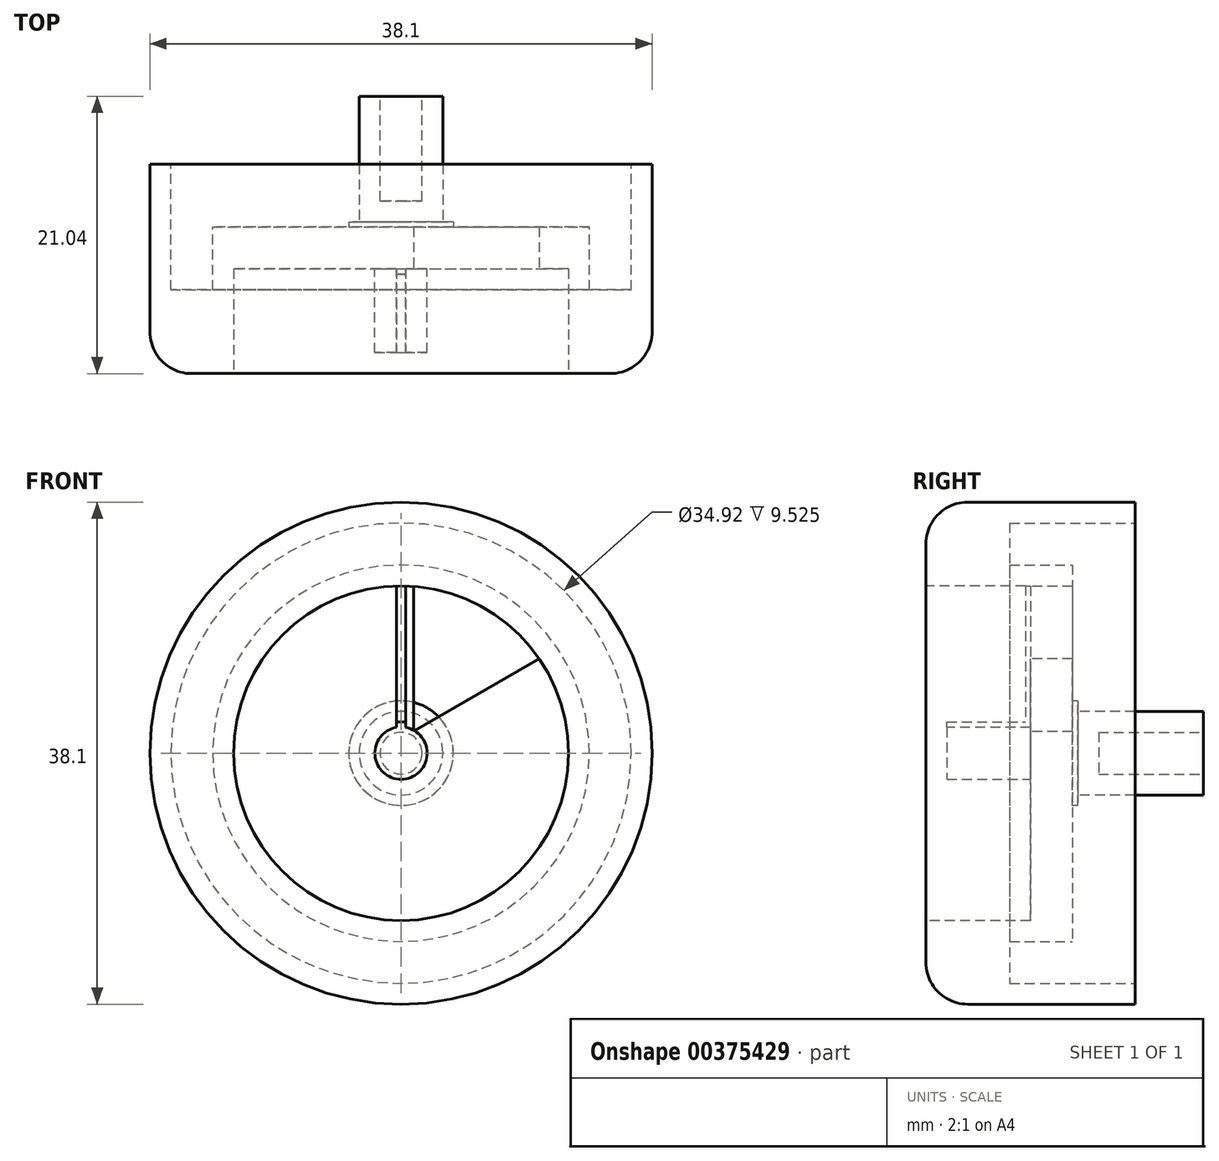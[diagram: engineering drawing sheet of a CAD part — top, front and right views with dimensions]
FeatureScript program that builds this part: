
annotation { "Feature Type Name" : "Feature", "Feature Type Description" : "" }
export const myFeature = defineFeature(function(context is Context, id is Id, definition is map)
    precondition{}
    {
        {
            var Q0;
            Q0=qCreatedBy(makeId("Front.planeOp"),FACE);
            var sketch = newSketch(context, id + "F0", { "sketchPlane" : qUnion([Q0])});
            skCircle(sketch, "E0", {"center": v(0, 0) * mm, "radius": 19.05 * mm});
            skSolve(sketch);
        }
        {
            var Q0;
            Q0=qSketchRegion(id+"F0",true);
            extrude(context, id + "F1", {"entities" : qUnion([Q0]), "depth" : 15.88 * mm, "symmetric" : true});
        }
        {
            var Q0;
            Q0=makeQuery(id+"F1.opExtrude","CAP_FACE",FACE,{"disambiguationData":[OSD([sQuery(id+"F0.wireOp",EDGE,"E0")])],"isStart":false});
            var sketch = newSketch(context, id + "F2", { "sketchPlane" : qUnion([Q0])});
            skCircle(sketch, "E1", {"center": v(0, 0) * mm, "radius": 12.7 * mm});
            skSolve(sketch);
        }
        {
            var Q0;
            Q0=qSketchRegion(id+"F2",true);
            extrude(context, id + "F3", {"entities" : qUnion([Q0]), "operationType" : NewBodyOperationType.REMOVE, "oppositeDirection" : true, "depth" : 7.94 * mm});
        }
        {
            var Q0;
            Q0=makeQuery(id+"F3.boolean.opBoolean","COPY",FACE,{"derivedFrom":makeQuery(id+"F3.opExtrude","CAP_FACE",FACE,{"disambiguationData":[OSD([sQuery(id+"F2.wireOp",EDGE,"E1")])],"isStart":false})});
            var sketch = newSketch(context, id + "F4", { "sketchPlane" : qUnion([Q0])});
            skLineSegment(sketch, "E2", {"start": v(0, 13.75) * mm, "end": v(0, 0) * mm, "construction": true});
            skLineSegment(sketch, "E3", {"start": v(0, 0) * mm, "end": v(12.12, 7) * mm, "construction": true});
            skLineSegment(sketch, "E4", {"start": v(0.95, 12.66) * mm, "end": v(0.95, 1.65) * mm});
            skLineSegment(sketch, "E5", {"start": v(0.95, 1.65) * mm, "end": v(10.5, 7.16) * mm});
            skArc(sketch, "E6.0", {"start": v(10.5, 7.16) * mm, "mid": v(6.35, 11) * mm, "end": v(0.95, 12.66) * mm});
            skLineSegment(sketch, "E7", {"start": v(0, 0) * mm, "end": v(9.55, 16.55) * mm, "construction": true});
            skSolve(sketch);
        }
        {
            var Q0;
            Q0=qSketchRegion(id+"F4",true);
            extrude(context, id + "F5", {"entities" : qUnion([Q0]), "operationType" : NewBodyOperationType.REMOVE, "endBound" : BoundingType.THROUGH_ALL, "oppositeDirection" : true, "depth" : 25.4 * mm});
        }
        {
            var Q0;
            Q0=makeQuery(id+"F1.opExtrude","CAP_FACE",FACE,{"disambiguationData":[OSD([sQuery(id+"F0.wireOp",EDGE,"E0")])],"isStart":true});
            var sketch = newSketch(context, id + "F6", { "sketchPlane" : qUnion([Q0])});
            skCircle(sketch, "E8", {"center": v(0, 0) * mm, "radius": 12.7 * mm});
            skSolve(sketch);
        }
        {
            var Q0;
            Q0=qSketchRegion(id+"F6",true);
            extrude(context, id + "F7", {"entities" : qUnion([Q0]), "operationType" : NewBodyOperationType.REMOVE, "oppositeDirection" : true, "depth" : 4.76 * mm});
        }
        {
            var Q0;
            Q0=makeQuery(id+"F7.boolean.opBoolean","COPY",FACE,{"derivedFrom":makeQuery(id+"F7.opExtrude","CAP_FACE",FACE,{"disambiguationData":[OSD([sQuery(id+"F6.wireOp",EDGE,"E8")])],"isStart":false})});
            var sketch = newSketch(context, id + "F8", { "sketchPlane" : qUnion([Q0])});
            skCircle(sketch, "E9", {"center": v(0, 0) * mm, "radius": 3.97 * mm});
            skSolve(sketch);
        }
        {
            var Q0;
            Q0=qSketchRegion(id+"F8",true);
            extrude(context, id + "F9", {"entities" : qUnion([Q0]), "operationType" : NewBodyOperationType.ADD, "depth" : 0.4 * mm});
        }
        {
            var Q0;
            Q0=makeQuery(id+"F9.opExtrude","CAP_FACE",FACE,{"disambiguationData":[OSD([sQuery(id+"F8.wireOp",EDGE,"E9")])],"isStart":false});
            var sketch = newSketch(context, id + "F10", { "sketchPlane" : qUnion([Q0])});
            skCircle(sketch, "E10", {"center": v(0, 0) * mm, "radius": 3.17 * mm});
            skSolve(sketch);
        }
        {
            var Q0;
            Q0=qSketchRegion(id+"F10",true);
            extrude(context, id + "F11", {"entities" : qUnion([Q0]), "operationType" : NewBodyOperationType.ADD, "depth" : 9.52 * mm});
        }
        {
            var Q0;
            Q0=makeQuery(id+"F11.opExtrude","CAP_FACE",FACE,{"disambiguationData":[OSD([sQuery(id+"F10.wireOp",EDGE,"E10")])],"isStart":false});
            var sketch = newSketch(context, id + "F12", { "sketchPlane" : qUnion([Q0])});
            skCircle(sketch, "E11", {"center": v(0, 0) * mm, "radius": 1.59 * mm});
            skSolve(sketch);
        }
        {
            var Q0;
            Q0=qSketchRegion(id+"F12",true);
            extrude(context, id + "F13", {"entities" : qUnion([Q0]), "operationType" : NewBodyOperationType.REMOVE, "oppositeDirection" : true, "depth" : 7.94 * mm});
        }
        {
            var Q0;
            Q0=makeQuery(id+"F3.boolean.opBoolean","COPY",FACE,{"derivedFrom":makeQuery(id+"F3.opExtrude","CAP_FACE",FACE,{"disambiguationData":[OSD([sQuery(id+"F2.wireOp",EDGE,"E1")])],"isStart":false})});
            var sketch = newSketch(context, id + "F14", { "sketchPlane" : qUnion([Q0])});
            skCircle(sketch, "E12", {"center": v(0, 0) * mm, "radius": 1.98 * mm});
            skSolve(sketch);
        }
        {
            var Q0;
            Q0=qSketchRegion(id+"F14",true);
            extrude(context, id + "F15", {"entities" : qUnion([Q0]), "operationType" : NewBodyOperationType.ADD, "depth" : 6.35 * mm});
        }
        {
            var Q0;
            {var subQ2=sQuery(id+"F2.wireOp",EDGE,"E1");Q0=makeQuery(id+"F15.boolean.opBoolean","SPLIT",FACE,{"disambiguationData":[TD([makeQuery(id+"F5.boolean.opBoolean","COPY",FACE,{"derivedFrom":makeQuery(id+"F5.opExtrude","SWEPT_FACE",FACE,{"disambiguationData":[OSD([sQuery(id+"F4.wireOp",EDGE,"E4")])]})})])],"derivedFrom":makeQuery(id+"F3.boolean.opBoolean","COPY",FACE,{"derivedFrom":makeQuery(id+"F3.opExtrude","CAP_FACE",FACE,{"disambiguationData":[OSD([subQ2])],"isStart":false})})});}
            var sketch = newSketch(context, id + "F16", { "sketchPlane" : qUnion([Q0])});
            skLineSegment(sketch, "E13.bottom", {"start": v(-0.34, 12.7) * mm, "end": v(0.34, 12.7) * mm});
            skLineSegment(sketch, "E13.top", {"start": v(-0.34, 2.37) * mm, "end": v(0.34, 2.37) * mm});
            skLineSegment(sketch, "E13.left", {"start": v(-0.34, 12.7) * mm, "end": v(-0.34, 2.37) * mm});
            skLineSegment(sketch, "E13.right", {"start": v(0.34, 12.7) * mm, "end": v(0.34, 2.37) * mm});
            skSolve(sketch);
        }
        {
            var Q0;
            {var subQ0=sQuery(id+"F16.wireOp",EDGE,"E13.left");var subQ1=sQuery(id+"F16.wireOp",EDGE,"E13.top");var subQ2=makeQuery(id+"F16.imprint","INTERSECT",VERTEX,{"derivedFrom":[subQ1,subQ0]});Q0=makeQuery(id+"F16.imprint","IMPRINT",FACE,{"disambiguationData":[TD([[makeQuery(id+"F16.imprint","IMPRINT",EDGE,{"disambiguationData":[TD([[subQ2,-1.0]])],"derivedFrom":subQ1}),1.0]])]});}
            extrude(context, id + "F17", {"entities" : qUnion([Q0]), "operationType" : NewBodyOperationType.ADD, "depth" : 0.4 * mm});
        }
        {
            var Q0;
            Q0=makeQuery(id+"F15.opExtrude","CAP_FACE",FACE,{"disambiguationData":[OSD([sQuery(id+"F14.wireOp",EDGE,"E12")])],"isStart":false});
            var sketch = newSketch(context, id + "F18", { "sketchPlane" : qUnion([Q0])});
            skLineSegment(sketch, "E14.bottom", {"start": v(-0.34, 1.95) * mm, "end": v(0.34, 1.95) * mm});
            skLineSegment(sketch, "E14.top", {"start": v(-0.34, 2.36) * mm, "end": v(0.34, 2.36) * mm});
            skLineSegment(sketch, "E14.left", {"start": v(-0.34, 1.95) * mm, "end": v(-0.34, 2.36) * mm});
            skLineSegment(sketch, "E14.right", {"start": v(0.34, 1.95) * mm, "end": v(0.34, 2.36) * mm});
            skSolve(sketch);
        }
        {
            var Q0;
            Q0=qSketchRegion(id+"F18",true);
            extrude(context, id + "F19", {"entities" : qUnion([Q0]), "operationType" : NewBodyOperationType.ADD, "oppositeDirection" : true, "depth" : 6.35 * mm});
        }
        {
            var Q0;
            Q0=makeQuery(id+"F1.opExtrude","CAP_FACE",FACE,{"disambiguationData":[OSD([sQuery(id+"F0.wireOp",EDGE,"E0")])],"isStart":true});
            var sketch = newSketch(context, id + "F20", { "sketchPlane" : qUnion([Q0])});
            skCircle(sketch, "E15", {"center": v(0, 0) * mm, "radius": 17.46 * mm});
            skSolve(sketch);
        }
        {
            var Q0;
            Q0=makeQuery(id+"F20.imprint","IMPRINT",FACE,{"disambiguationData":[TD([[makeQuery(id+"F20.imprint","IMPRINT",EDGE,{"derivedFrom":sQuery(id+"F20.wireOp",EDGE,"E15")}),1.0]])]});
            var sketch = newSketch(context, id + "F21", { "sketchPlane" : qUnion([Q0])});
            skCircle(sketch, "E16.0", {"center": v(0, 0) * mm, "radius": 12.7 * mm});
            skCircle(sketch, "E17.0", {"center": v(0, 0) * mm, "radius": 17.46 * mm});
            skSolve(sketch);
        }
        {
            var Q0;
            Q0=qSketchRegion(id+"F21",true);
            var Q1;
            Q1=makeQuery(id+"F20.imprint","IMPRINT",FACE,{"disambiguationData":[TD([[makeQuery(id+"F20.imprint","IMPRINT",EDGE,{"derivedFrom":sQuery(id+"F20.wireOp",EDGE,"E15")}),1.0]])]});
            var Q2;
            {var subQ2=sQuery(id+"F6.wireOp",EDGE,"E8");Q2=makeQuery(id+"F9.boolean.opBoolean","SPLIT",FACE,{"disambiguationData":[TD([makeQuery(id+"FinYMH1RS6XASPV_1.4.F5.boolean.opBoolean","COPY",FACE,{"derivedFrom":makeQuery(id+"FinYMH1RS6XASPV_1.4.F5.opExtrude","SWEPT_FACE",FACE,{"disambiguationData":[OSD([sQuery(id+"F4.wireOp",EDGE,"E5")])]})})])],"derivedFrom":makeQuery(id+"F7.boolean.opBoolean","COPY",FACE,{"derivedFrom":makeQuery(id+"F7.opExtrude","CAP_FACE",FACE,{"disambiguationData":[OSD([subQ2])],"isStart":false})})});}
            extrude(context, id + "F22", {"entities" : qUnion([Q0, Q1]), "operationType" : NewBodyOperationType.REMOVE, "endBound" : BoundingType.UP_TO_SURFACE, "oppositeDirection" : true, "endBoundEntityFace" : qUnion([Q2]), "depth" : 25.4 * mm});
        }
        {
            var Q0;
            {var subQ4=sQuery(id+"F4.wireOp",EDGE,"E5");var subQ9=sQuery(id+"F6.wireOp",EDGE,"E8");var subQ11=sQuery(id+"F4.wireOp",EDGE,"E4");var subQ15=makeQuery(id+"F7.boolean.opBoolean","COPY",FACE,{"derivedFrom":makeQuery(id+"F7.opExtrude","CAP_FACE",FACE,{"disambiguationData":[OSD([subQ9])],"isStart":false})});Q0=makeQuery(id+"F22.boolean.opBoolean","MERGE",FACE,{"derivedFrom":[makeQuery(id+"F9.boolean.opBoolean","SPLIT",FACE,{"disambiguationData":[TD([makeQuery(id+"F5.boolean.opBoolean","COPY",FACE,{"derivedFrom":makeQuery(id+"F5.opExtrude","SWEPT_FACE",FACE,{"disambiguationData":[OSD([subQ11])]})})])],"derivedFrom":subQ15}),makeQuery(id+"F9.boolean.opBoolean","SPLIT",FACE,{"disambiguationData":[TD([makeQuery(id+"F5.boolean.opBoolean","COPY",FACE,{"derivedFrom":makeQuery(id+"F5.opExtrude","SWEPT_FACE",FACE,{"disambiguationData":[OSD([subQ4])]})})])],"derivedFrom":subQ15}),makeQuery(id+"F9.boolean.opBoolean","SPLIT",FACE,{"disambiguationData":[TD([makeQuery(id+"FinYMH1RS6XASPV_1.1.F5.boolean.opBoolean","COPY",FACE,{"derivedFrom":makeQuery(id+"FinYMH1RS6XASPV_1.1.F5.opExtrude","SWEPT_FACE",FACE,{"disambiguationData":[OSD([subQ4])]})})])],"derivedFrom":subQ15}),makeQuery(id+"F9.boolean.opBoolean","SPLIT",FACE,{"disambiguationData":[TD([makeQuery(id+"FinYMH1RS6XASPV_1.2.F5.boolean.opBoolean","COPY",FACE,{"derivedFrom":makeQuery(id+"FinYMH1RS6XASPV_1.2.F5.opExtrude","SWEPT_FACE",FACE,{"disambiguationData":[OSD([subQ4])]})})])],"derivedFrom":subQ15}),makeQuery(id+"F9.boolean.opBoolean","SPLIT",FACE,{"disambiguationData":[TD([makeQuery(id+"FinYMH1RS6XASPV_1.3.F5.boolean.opBoolean","COPY",FACE,{"derivedFrom":makeQuery(id+"FinYMH1RS6XASPV_1.3.F5.opExtrude","SWEPT_FACE",FACE,{"disambiguationData":[OSD([subQ4])]})})])],"derivedFrom":subQ15}),makeQuery(id+"F9.boolean.opBoolean","SPLIT",FACE,{"disambiguationData":[TD([makeQuery(id+"FinYMH1RS6XASPV_1.4.F5.boolean.opBoolean","COPY",FACE,{"derivedFrom":makeQuery(id+"FinYMH1RS6XASPV_1.4.F5.opExtrude","SWEPT_FACE",FACE,{"disambiguationData":[OSD([subQ4])]})})])],"derivedFrom":subQ15}),makeQuery(id+"F22.opExtrude","CAP_FACE",FACE,{"disambiguationData":[OSD([sQuery(id+"F21.wireOp",EDGE,"E16.0"),sQuery(id+"F21.wireOp",EDGE,"E17.0")])],"isStart":false})]});}
            var sketch = newSketch(context, id + "F23", { "sketchPlane" : qUnion([Q0])});
            skCircle(sketch, "E18", {"center": v(0, 0) * mm, "radius": 14.29 * mm});
            skSolve(sketch);
        }
        {
            var Q0;
            Q0=makeQuery(id+"F23.imprint","IMPRINT",FACE,{"disambiguationData":[TD([[makeQuery(id+"F23.imprint","IMPRINT",EDGE,{"derivedFrom":sQuery(id+"F23.wireOp",EDGE,"E18")}),-1.0]])]});
            var sketch = newSketch(context, id + "F24", { "sketchPlane" : qUnion([Q0])});
            skCircle(sketch, "E19.0", {"center": v(0, 0) * mm, "radius": 14.29 * mm});
            skCircle(sketch, "E20.0", {"center": v(0, 0) * mm, "radius": 17.46 * mm});
            skSolve(sketch);
        }
        {
            var Q0;
            Q0=qSketchRegion(id+"F24",true);
            extrude(context, id + "F25", {"entities" : qUnion([Q0]), "operationType" : NewBodyOperationType.REMOVE, "oppositeDirection" : true, "depth" : 4.76 * mm});
        }
        {
            var Q0;
            Q0=makeQuery(id+"F1.opExtrude","CAP_EDGE",EDGE,{"disambiguationData":[OSD([sQuery(id+"F0.wireOp",EDGE,"E0")])],"isStart":false});
            var Q1;
            Q1=makeQuery(id+"F3.boolean.opBoolean","COPY",EDGE,{"derivedFrom":makeQuery(id+"F3.opExtrude","CAP_EDGE",EDGE,{"disambiguationData":[OSD([sQuery(id+"F2.wireOp",EDGE,"E1")])],"isStart":true})});
            fillet(context, id + "F26", {"entities" : qUnion([Q0, Q1]), "radius" : 3.17 * mm, "tangentPropagation" : true, "allowEdgeOverflow" : false});
        }
    });
